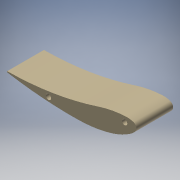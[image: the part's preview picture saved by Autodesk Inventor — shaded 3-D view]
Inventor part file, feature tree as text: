
AUTODESK INVENTOR PART (.ipt)
format: ipt  version: 2018 (Build 220112000, 112)  size: 113,664 bytes
history: native  units: mm
features: extrude x1, sketch x1, projected_geometry x1
ambient origin geometry x8: Origin, YZ Plane, XZ Plane, XY Plane, X Axis, Y Axis, Z Axis, Center Point
bodies: Body1 (feature_tree)
feature tree (3):
  extrude  "押し出し1"  Depth=41.5mm TaperAngle=0.0deg
  sketch  "スケッチ1"
  projected_geometry  "投影ループ1"
